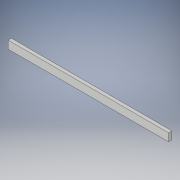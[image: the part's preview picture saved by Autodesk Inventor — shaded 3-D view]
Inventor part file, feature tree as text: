
AUTODESK INVENTOR PART (.ipt)
format: ipt  version: 2017 (Build 210142000, 142)  size: 92,160 bytes
history: native  units: in
note: dims shown in document units (in); Inventor stores cm internally (conversion verified against a paired STEP export)
features: extrude x1, sketch x1
ambient origin geometry x8: Origin, YZ Plane, XZ Plane, XY Plane, X Axis, Y Axis, Z Axis, Center Point
bodies: Solid1 (feature_tree)
feature tree (2):
  extrude  "Extrusion1"  Depth=3.5in
  sketch  "Sketch1"  dims[d0=72.0in d1=3.5in d2=1.5in d3=0.0in]
